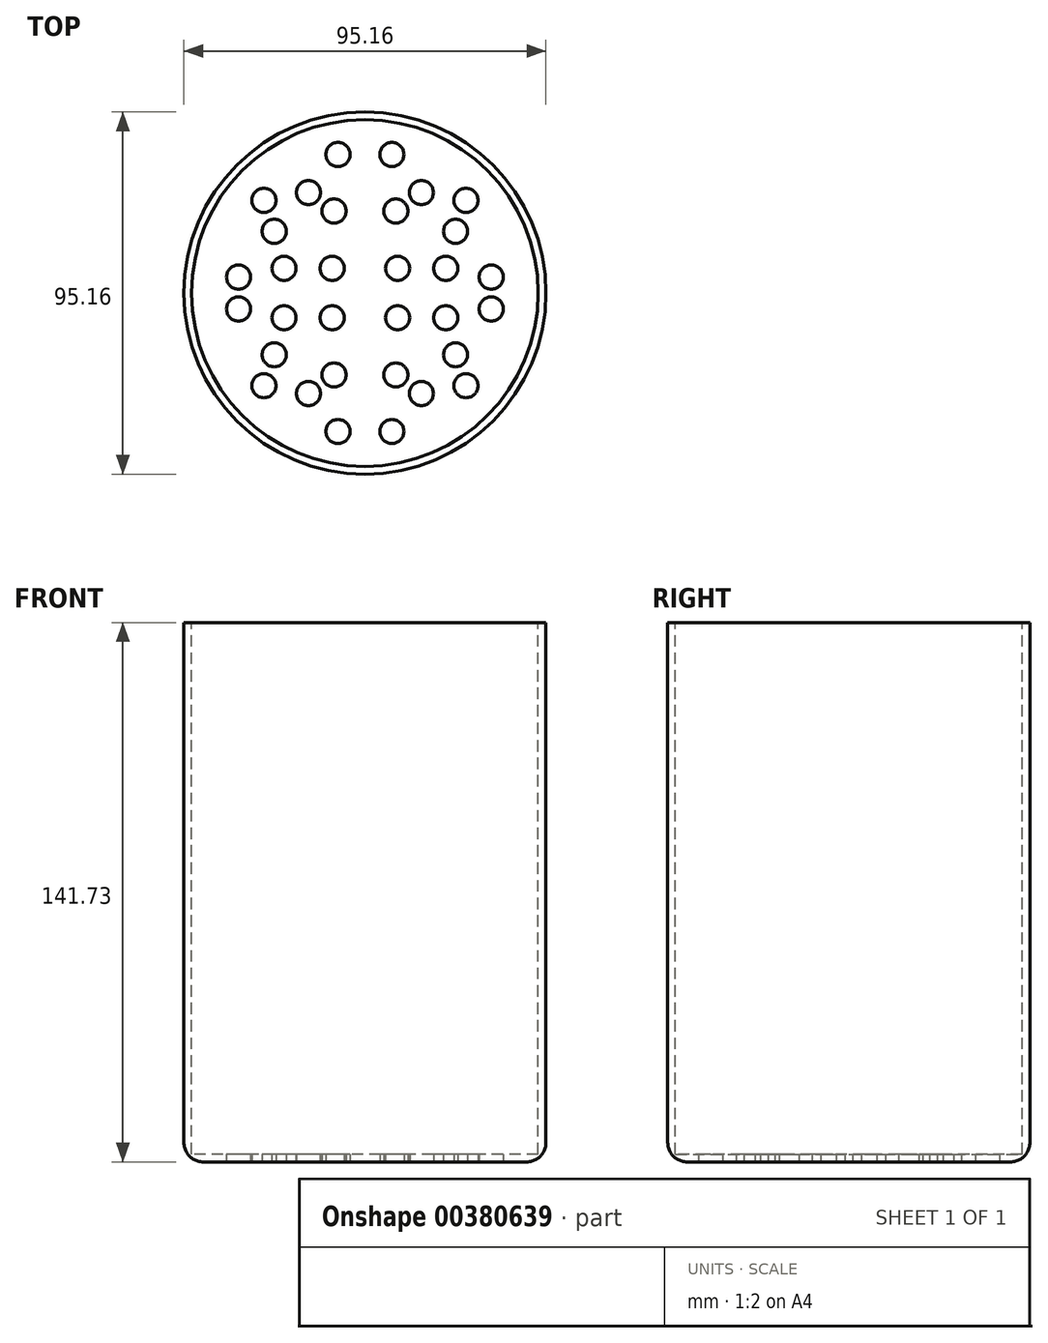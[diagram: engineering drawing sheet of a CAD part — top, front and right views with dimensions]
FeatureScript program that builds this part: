
annotation { "Feature Type Name" : "Feature", "Feature Type Description" : "" }
export const myFeature = defineFeature(function(context is Context, id is Id, definition is map)
    precondition{}
    {
        {
            var Q0;
            Q0=qCreatedBy(makeId("Top.planeOp"),FACE);
            var sketch = newSketch(context, id + "F0", { "sketchPlane" : qUnion([Q0])});
            skCircle(sketch, "E0", {"center": v(0, 0) * mm, "radius": 45.54 * mm});
            skSolve(sketch);
        }
        {
            var Q0;
            Q0 = qSketchRegion(id + "F0", true);
            extrude(context, id + "F1", {"entities" : qUnion([Q0]), "oppositeDirection" : true, "depth" : 139.7 * mm});
        }
        {
            var Q0;
            Q0=makeQuery(id+"F1.opExtrude","CAP_FACE",FACE,{"disambiguationData":[OSD([sQuery(id+"F0.wireOp",EDGE,"E0")])],"isStart":true});
            shell(context, id + "F2", {"entities" : qUnion([Q0]), "thickness" : 2.03 * mm, "oppositeDirection" : true});
        }
        {
            var Q0;
            Q0=makeQuery(id+"F1.opExtrude","CAP_EDGE",EDGE,{"disambiguationData":[OSD([sQuery(id+"F0.wireOp",EDGE,"E0")])],"isStart":false});
            fillet(context, id + "F3", {"entities" : qUnion([Q0]), "radius" : 5.08 * mm, "tangentPropagation" : true, "allowEdgeOverflow" : false});
        }
        {
            var Q0;
            Q0=makeQuery(id+"F1.opExtrude","CAP_FACE",FACE,{"disambiguationData":[OSD([sQuery(id+"F0.wireOp",EDGE,"E0")])],"isStart":false});
            var sketch = newSketch(context, id + "F4", { "sketchPlane" : qUnion([Q0])});
            skLineSegment(sketch, "E1", {"start": v(0, -42.5) * mm, "end": v(0, 42.5) * mm});
            skLineSegment(sketch, "E2", {"start": v(0, 0) * mm, "end": v(42.5, 0) * mm});
            skLineSegment(sketch, "E3", {"start": v(42.5, 0) * mm, "end": v(0, 0) * mm});
            skLineSegment(sketch, "E4", {"start": v(0, 0) * mm, "end": v(-42.5, 0) * mm});
            skPoint(sketch, "E5", {"position": v(-7.08, 36.39) * mm});
            skPoint(sketch, "E6", {"position": v(-26.55, 24.35) * mm});
            skPoint(sketch, "E7", {"position": v(-33.2, 4.2) * mm});
            skPoint(sketch, "E8", {"position": v(-8.12, 21.53) * mm});
            skPoint(sketch, "E9", {"position": v(-21.25, 6.5) * mm});
            skPoint(sketch, "E10", {"position": v(-8.6, 6.5) * mm});
            skPoint(sketch, "E11", {"position": v(-21.25, 0) * mm});
            skPoint(sketch, "E12", {"position": v(-23.83, 16.22) * mm});
            skPoint(sketch, "E13", {"position": v(-14.83, 26.4) * mm});
            skLineSegment(sketch, "E14.MirrorCS", {"start": v(-42.5, 0) * mm, "end": v(0, 0) * mm});
            skPoint(sketch, "E15.MirrorP", {"position": v(8.6, 6.5) * mm});
            skPoint(sketch, "E16.MirrorP", {"position": v(8.12, 21.53) * mm});
            skPoint(sketch, "E17.MirrorP", {"position": v(21.25, 6.5) * mm});
            skPoint(sketch, "E18.MirrorP", {"position": v(33.2, 4.2) * mm});
            skPoint(sketch, "E19.MirrorP", {"position": v(26.55, 24.35) * mm});
            skPoint(sketch, "E20.MirrorP", {"position": v(23.83, 16.22) * mm});
            skPoint(sketch, "E21.MirrorP", {"position": v(14.83, 26.4) * mm});
            skPoint(sketch, "E22.MirrorP", {"position": v(7.08, 36.39) * mm});
            skPoint(sketch, "E23.MirrorP", {"position": v(8.6, -6.5) * mm});
            skPoint(sketch, "E24.MirrorP", {"position": v(21.25, -6.5) * mm});
            skPoint(sketch, "E25.MirrorP", {"position": v(33.2, -4.2) * mm});
            skPoint(sketch, "E26.MirrorP", {"position": v(23.83, -16.22) * mm});
            skPoint(sketch, "E27.MirrorP", {"position": v(26.55, -24.35) * mm});
            skPoint(sketch, "E28.MirrorP", {"position": v(14.83, -26.4) * mm});
            skPoint(sketch, "E29.MirrorP", {"position": v(8.12, -21.53) * mm});
            skPoint(sketch, "E30.MirrorP", {"position": v(7.08, -36.39) * mm});
            skPoint(sketch, "E31.MirrorP", {"position": v(-7.08, -36.39) * mm});
            skPoint(sketch, "E32.MirrorP", {"position": v(-14.83, -26.4) * mm});
            skPoint(sketch, "E33.MirrorP", {"position": v(-8.12, -21.53) * mm});
            skPoint(sketch, "E34.MirrorP", {"position": v(-26.55, -24.35) * mm});
            skPoint(sketch, "E35.MirrorP", {"position": v(-23.83, -16.22) * mm});
            skPoint(sketch, "E36.MirrorP", {"position": v(-21.25, -6.5) * mm});
            skPoint(sketch, "E37.MirrorP", {"position": v(-33.2, -4.2) * mm});
            skPoint(sketch, "E38.MirrorP", {"position": v(-8.6, -6.5) * mm});
            skSolve(sketch);
        }
        {
            var Q0;
            Q0=sQuery(id+"F4.wireOp",VERTEX,"E10");
            var Q1;
            Q1=sQuery(id+"F4.wireOp",VERTEX,"E8");
            var Q2;
            Q2=sQuery(id+"F4.wireOp",VERTEX,"E13");
            var Q3;
            Q3=sQuery(id+"F4.wireOp",VERTEX,"E5");
            var Q4;
            Q4=sQuery(id+"F4.wireOp",VERTEX,"E6");
            var Q5;
            Q5=sQuery(id+"F4.wireOp",VERTEX,"E12");
            var Q6;
            Q6=sQuery(id+"F4.wireOp",VERTEX,"E9");
            var Q7;
            Q7=sQuery(id+"F4.wireOp",VERTEX,"E7");
            var Q8;
            Q8=makeQuery(id+"F1.opExtrude","SWEPT_BODY",BODY,{"disambiguationData":[OSD([sQuery(id+"F0.wireOp",EDGE,"E0")])]});
            hole(context, id + "F5", {"style" : HoleStyle.SIMPLE, "endStyle" : HoleEndStyle.THROUGH, "holeDiameter" : 6.35 * mm, "isTappedThrough" : true, "tappedDepth" : 12.7 * mm, "tapClearance" : 3, "locations" : qUnion([Q0, Q1, Q2, Q3, Q4, Q5, Q6, Q7]), "scope" : qUnion([Q8])});
        }
        {
            var Q0;
            Q0=sQuery(id+"F4.wireOp",VERTEX,"E15.MirrorP");
            var Q1;
            Q1=sQuery(id+"F4.wireOp",VERTEX,"E17.MirrorP");
            var Q2;
            Q2=sQuery(id+"F4.wireOp",VERTEX,"E18.MirrorP");
            var Q3;
            Q3=sQuery(id+"F4.wireOp",VERTEX,"E16.MirrorP");
            var Q4;
            Q4=sQuery(id+"F4.wireOp",VERTEX,"E21.MirrorP");
            var Q5;
            Q5=sQuery(id+"F4.wireOp",VERTEX,"E22.MirrorP");
            var Q6;
            Q6=sQuery(id+"F4.wireOp",VERTEX,"E20.MirrorP");
            var Q7;
            Q7=sQuery(id+"F4.wireOp",VERTEX,"E19.MirrorP");
            var Q8;
            Q8=makeQuery(id+"F1.opExtrude","SWEPT_BODY",BODY,{"disambiguationData":[OSD([sQuery(id+"F0.wireOp",EDGE,"E0")])]});
            hole(context, id + "F6", {"style" : HoleStyle.SIMPLE, "endStyle" : HoleEndStyle.THROUGH, "holeDiameter" : 6.35 * mm, "isTappedThrough" : true, "tappedDepth" : 12.7 * mm, "tapClearance" : 3, "locations" : qUnion([Q0, Q1, Q2, Q3, Q4, Q5, Q6, Q7]), "scope" : qUnion([Q8])});
        }
        {
            var Q0;
            Q0=sQuery(id+"F4.wireOp",VERTEX,"E37.MirrorP");
            var Q1;
            Q1=sQuery(id+"F4.wireOp",VERTEX,"E38.MirrorP");
            var Q2;
            Q2=sQuery(id+"F4.wireOp",VERTEX,"E36.MirrorP");
            var Q3;
            Q3=sQuery(id+"F4.wireOp",VERTEX,"E33.MirrorP");
            var Q4;
            Q4=sQuery(id+"F4.wireOp",VERTEX,"E32.MirrorP");
            var Q5;
            Q5=sQuery(id+"F4.wireOp",VERTEX,"E31.MirrorP");
            var Q6;
            Q6=sQuery(id+"F4.wireOp",VERTEX,"E34.MirrorP");
            var Q7;
            Q7=sQuery(id+"F4.wireOp",VERTEX,"E35.MirrorP");
            var Q8;
            Q8=sQuery(id+"F4.wireOp",VERTEX,"E23.MirrorP");
            var Q9;
            Q9=sQuery(id+"F4.wireOp",VERTEX,"E25.MirrorP");
            var Q10;
            Q10=sQuery(id+"F4.wireOp",VERTEX,"E24.MirrorP");
            var Q11;
            Q11=sQuery(id+"F4.wireOp",VERTEX,"E26.MirrorP");
            var Q12;
            Q12=sQuery(id+"F4.wireOp",VERTEX,"E27.MirrorP");
            var Q13;
            Q13=sQuery(id+"F4.wireOp",VERTEX,"E28.MirrorP");
            var Q14;
            Q14=sQuery(id+"F4.wireOp",VERTEX,"E29.MirrorP");
            var Q15;
            Q15=sQuery(id+"F4.wireOp",VERTEX,"E30.MirrorP");
            var Q16;
            Q16=makeQuery(id+"F1.opExtrude","SWEPT_BODY",BODY,{"disambiguationData":[OSD([sQuery(id+"F0.wireOp",EDGE,"E0")])]});
            hole(context, id + "F7", {"style" : HoleStyle.SIMPLE, "endStyle" : HoleEndStyle.THROUGH, "holeDiameter" : 6.35 * mm, "isTappedThrough" : true, "tappedDepth" : 12.7 * mm, "tapClearance" : 3, "locations" : qUnion([Q0, Q1, Q2, Q3, Q4, Q5, Q6, Q7, Q8, Q9, Q10, Q11, Q12, Q13, Q14, Q15]), "scope" : qUnion([Q16])});
        }
    });
